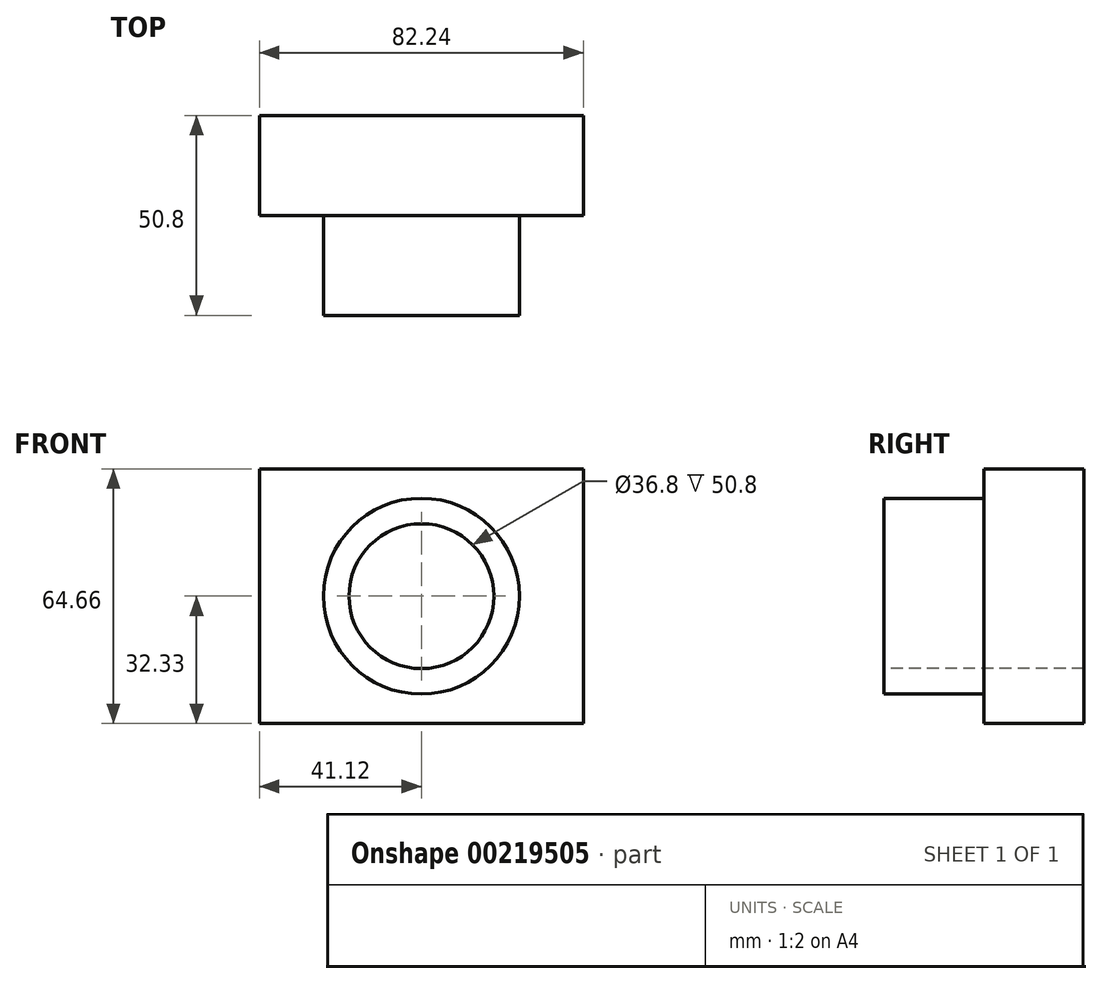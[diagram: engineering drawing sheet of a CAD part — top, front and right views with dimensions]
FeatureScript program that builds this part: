
annotation { "Feature Type Name" : "Feature", "Feature Type Description" : "" }
export const myFeature = defineFeature(function(context is Context, id is Id, definition is map)
    precondition{}
    {
        {
            var Q0;
            Q0=qCreatedBy(makeId("Front.planeOp"),FACE);
            var sketch = newSketch(context, id + "F0", { "sketchPlane" : qUnion([Q0])});
            skLineSegment(sketch, "E0.bottom", {"start": v(-41.12, 32.33) * mm, "end": v(41.12, 32.33) * mm});
            skLineSegment(sketch, "E0.top", {"start": v(-41.12, -32.33) * mm, "end": v(41.12, -32.33) * mm});
            skLineSegment(sketch, "E0.left", {"start": v(-41.12, 32.33) * mm, "end": v(-41.12, -32.33) * mm});
            skLineSegment(sketch, "E0.right", {"start": v(41.12, 32.33) * mm, "end": v(41.12, -32.33) * mm});
            skPoint(sketch, "E0.middle", {"position": v(0, 0) * mm});
            skSolve(sketch);
        }
        {
            var Q0;
            Q0 = qSketchRegion(id + "F0", true);
            extrude(context, id + "F1", {"entities" : qUnion([Q0]), "depth" : 25.4 * mm});
        }
        {
            var Q0;
            Q0=makeQuery(id+"F1.opExtrude","CAP_FACE",FACE,{"disambiguationData":[OSD([sQuery(id+"F0.wireOp",EDGE,"E0.bottom"),sQuery(id+"F0.wireOp",EDGE,"E0.top"),sQuery(id+"F0.wireOp",EDGE,"E0.left"),sQuery(id+"F0.wireOp",EDGE,"E0.right")])],"isStart":false});
            var sketch = newSketch(context, id + "F2", { "sketchPlane" : qUnion([Q0])});
            skCircle(sketch, "E1", {"center": v(0, 0) * mm, "radius": 24.88 * mm});
            skSolve(sketch);
        }
        {
            var Q0;
            Q0 = qSketchRegion(id + "F2", true);
            extrude(context, id + "F3", {"entities" : qUnion([Q0]), "operationType" : NewBodyOperationType.ADD, "depth" : 25.4 * mm});
        }
        {
            var Q0;
            Q0=makeQuery(id+"F3.opExtrude","CAP_FACE",FACE,{"disambiguationData":[OSD([sQuery(id+"F2.wireOp",EDGE,"E1")])],"isStart":false});
            var sketch = newSketch(context, id + "F4", { "sketchPlane" : qUnion([Q0])});
            skCircle(sketch, "E2", {"center": v(0, 0) * mm, "radius": 18.4 * mm});
            skSolve(sketch);
        }
        {
            var Q0;
            Q0 = qSketchRegion(id + "F4", true);
            extrude(context, id + "F5", {"entities" : qUnion([Q0]), "operationType" : NewBodyOperationType.REMOVE, "oppositeDirection" : true, "depth" : 127 * mm});
        }
    });
